# Revit family: ГРЕЕРС Д1
name_source: partatom
category: Modele ogólne
revit_build: Autodesk Revit 2016 (Build: 20150220_1215(x64)
units: mm (PartAtom-declared; Revit-internal decimal feet)

## family parameters
Może być obiektem nadrzędnym dla zbrojenia = Nie
Obiekt nadrzędny = Powierzchnia
Punkt obliczania pomieszczeń = Nie
Tnij formami wycięć po wczytaniu = Nie
Typ części = Normalny
Współdzielony = Nie
Wymiar okrągłego złącza = Użyj średnicy

## types (3) — shared parameters
IP = 54
Model = ГРЕЕРС Д1
Opis = Дестратификатор воздуха
Дестратификатор воздуха
Opis indeksowy = Дестратификатор ГРЕЕРС Д1 производительностью до 2500 м3/ч
Producent = ГРЕЕРС
URL = www.greers.ru
Вентилятор = Осевой, однофазный, переменного тока с 3-скоростным вентилятором
Осевой, однофазный, переменного тока с 3-скоростным вентилятором
Вес аппарата = 8.90 kg
Данные продукта = https://greers.ru
Индекс = 22100
Классификация нагрузки = ДВИГАТЕЛЬ
Коэффициент мощности = 1
Материал = ГРЕЕРС-EPP-черный
Напряжение питания = 230 V
Расстояние от перекрытия = 1000 mm  [stored 3.28084 ft]
Стандартное оснащение = Отсутствие
Управление = Включи/Выключи
zero-valued in all types: Domyślna rzędna

## per-type parameters (varying)
| type | Макс. потребление тока | Полная мощность | Производительность |
| ГРЕЕР Д1, 1 скорость | 0 A | 69 VA | 1500.0 m³/h |
| ГРЕЕР Д1, 2 скорость | 0 A | 92 VA | 2000.0 m³/h |
| ГРЕЕР Д1, 3 скорость | 1 A | 115 VA | 2500.0 m³/h |

note: [stored X ft] marks values corroborated as IEEE doubles in the binary element streams (Revit-internal decimal feet)
